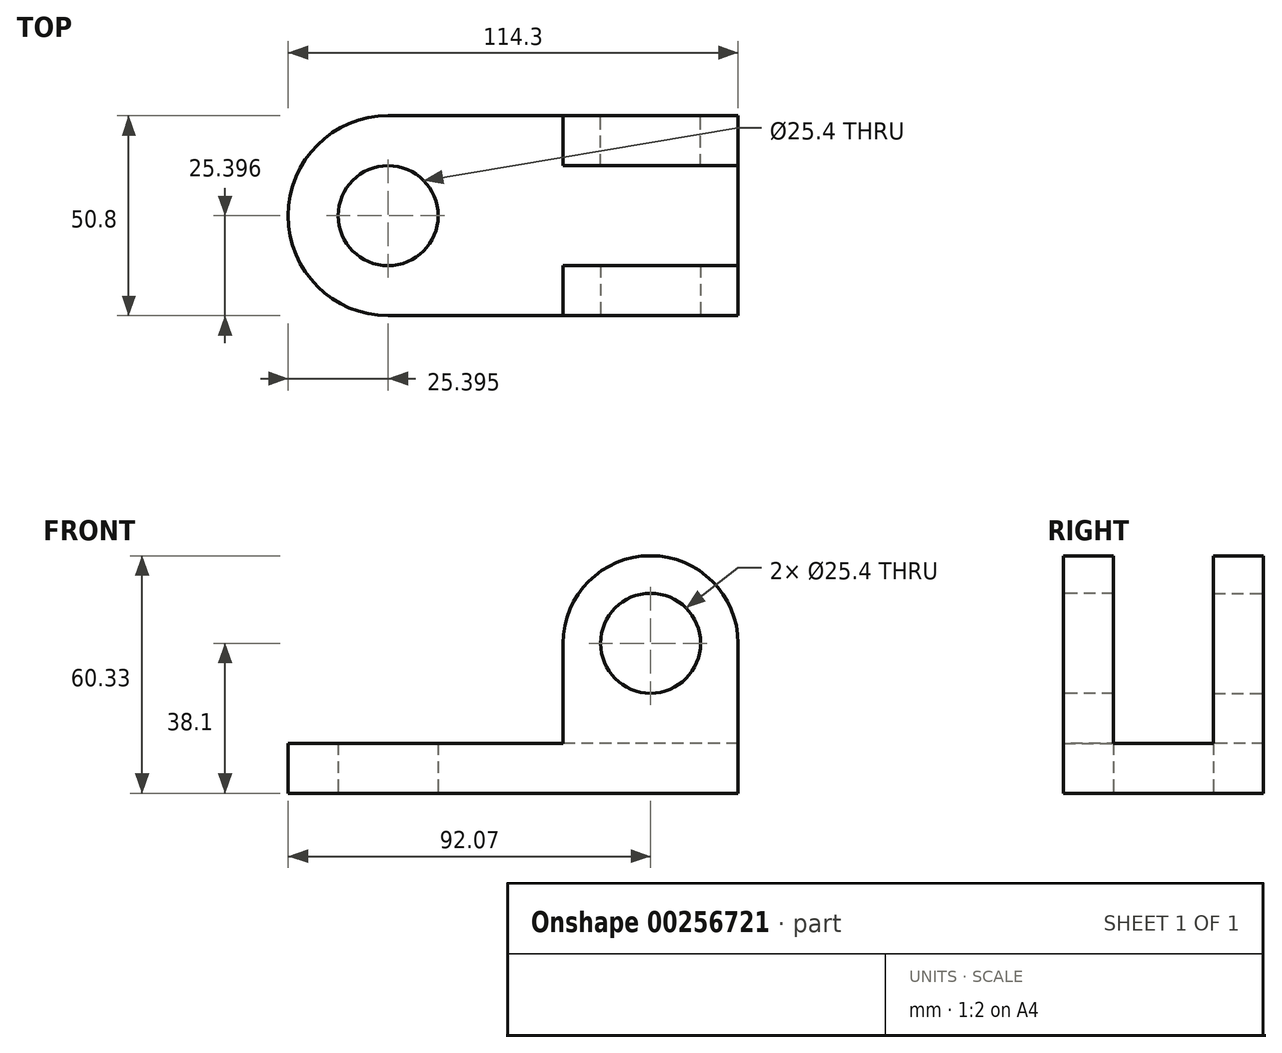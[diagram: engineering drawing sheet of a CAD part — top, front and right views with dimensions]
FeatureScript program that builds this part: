
annotation { "Feature Type Name" : "Feature", "Feature Type Description" : "" }
export const myFeature = defineFeature(function(context is Context, id is Id, definition is map)
    precondition{}
    {
        {
            var Q0;
            Q0=qCreatedBy(makeId("Top.planeOp"),FACE);
            var sketch = newSketch(context, id + "F0", { "sketchPlane" : qUnion([Q0])});
            skLineSegment(sketch, "E0.bottom", {"start": v(50.44, -47.27) * mm, "end": v(-38.46, -47.27) * mm});
            skLineSegment(sketch, "E0.top", {"start": v(50.44, 3.53) * mm, "end": v(-38.46, 3.53) * mm});
            skLineSegment(sketch, "E0.left", {"start": v(50.44, -47.27) * mm, "end": v(50.44, 3.53) * mm});
            skLineSegment(sketch, "E0.right", {"start": v(-38.46, -47.27) * mm, "end": v(-38.46, 3.53) * mm});
            skArc(sketch, "E1", {"start": v(-38.46, 3.53) * mm, "mid": v(-63.86, -21.87) * mm, "end": v(-38.46, -47.27) * mm});
            skCircle(sketch, "E2", {"center": v(-38.46, -21.87) * mm, "radius": 12.7 * mm});
            skSolve(sketch);
        }
        {
            var Q0;
            {var subQ0=sQuery(id+"F0.wireOp",EDGE,"E1");Q0=makeQuery(id+"F0.imprint","IMPRINT",FACE,{"disambiguationData":[TD([[makeQuery(id+"F0.imprint","IMPRINT",EDGE,{"derivedFrom":subQ0}),1.0]])]});}
            extrude(context, id + "F1", {"entities" : qUnion([Q0]), "depth" : 12.7 * mm});
        }
        {
            var Q0;
            {var subQ2=sQuery(id+"F0.wireOp",EDGE,"E0.bottom");Q0=makeQuery(id+"F0.imprint","IMPRINT",FACE,{"disambiguationData":[TD([[makeQuery(id+"F0.imprint","IMPRINT",EDGE,{"derivedFrom":subQ2}),-1.0]])]});}
            extrude(context, id + "F2", {"entities" : qUnion([Q0]), "operationType" : NewBodyOperationType.ADD, "depth" : 12.7 * mm});
        }
        {
            var Q0;
            {var subQ0=sQuery(id+"F0.wireOp",EDGE,"E2");var subQ1=sQuery(id+"F0.wireOp",EDGE,"E0.right");Q0=makeQuery(id+"F2.boolean.opBoolean","MERGE",FACE,{"derivedFrom":[makeQuery(id+"F1.opExtrude","CAP_FACE",FACE,{"disambiguationData":[OSD([subQ1,sQuery(id+"F0.wireOp",EDGE,"E1"),subQ0])],"isStart":false}),makeQuery(id+"F2.opExtrude","CAP_FACE",FACE,{"disambiguationData":[OSD([sQuery(id+"F0.wireOp",EDGE,"E0.bottom"),sQuery(id+"F0.wireOp",EDGE,"E0.top"),sQuery(id+"F0.wireOp",EDGE,"E0.left"),subQ1,subQ0])],"isStart":false})]});}
            var sketch = newSketch(context, id + "F3", { "sketchPlane" : qUnion([Q0])});
            skLineSegment(sketch, "E3", {"start": v(50.44, -21.87) * mm, "end": v(-25.76, -21.87) * mm});
            skLineSegment(sketch, "E4.bottom", {"start": v(50.44, -47.27) * mm, "end": v(5.99, -47.27) * mm});
            skLineSegment(sketch, "E4.top", {"start": v(50.44, -34.57) * mm, "end": v(5.99, -34.57) * mm});
            skLineSegment(sketch, "E4.left", {"start": v(50.44, -47.27) * mm, "end": v(50.44, -34.57) * mm});
            skLineSegment(sketch, "E4.right", {"start": v(5.99, -47.27) * mm, "end": v(5.99, -34.57) * mm});
            skLineSegment(sketch, "E5.MirrorCS", {"start": v(50.44, -9.17) * mm, "end": v(5.99, -9.17) * mm});
            skLineSegment(sketch, "E6.MirrorCS", {"start": v(5.99, 3.53) * mm, "end": v(5.99, -9.17) * mm});
            skLineSegment(sketch, "E7.MirrorCS", {"start": v(50.44, 3.53) * mm, "end": v(5.99, 3.53) * mm});
            skLineSegment(sketch, "E8.MirrorCS", {"start": v(50.44, 3.53) * mm, "end": v(50.44, -9.17) * mm});
            skSolve(sketch);
        }
        {
            var Q0;
            Q0=makeQuery(id+"F3.imprint","IMPRINT",FACE,{"disambiguationData":[TD([[makeQuery(id+"F3.imprint","IMPRINT",EDGE,{"derivedFrom":sQuery(id+"F3.wireOp",EDGE,"E4.bottom")}),-1.0]])]});
            extrude(context, id + "F4", {"entities" : qUnion([Q0]), "operationType" : NewBodyOperationType.ADD, "depth" : 25.4 * mm});
        }
        {
            var Q0;
            Q0=makeQuery(id+"F4.boolean.opBoolean","MERGE",FACE,{"derivedFrom":[makeQuery(id+"F2.opExtrude","SWEPT_FACE",FACE,{"disambiguationData":[OSD([sQuery(id+"F0.wireOp",EDGE,"E0.bottom")])]}),makeQuery(id+"F4.opExtrude","SWEPT_FACE",FACE,{"disambiguationData":[OSD([sQuery(id+"F3.wireOp",EDGE,"E4.bottom")])]})]});
            var sketch = newSketch(context, id + "F5", { "sketchPlane" : qUnion([Q0])});
            skArc(sketch, "E9", {"start": v(50.44, 38.1) * mm, "mid": v(28.21, 60.32) * mm, "end": v(5.99, 38.1) * mm});
            skSolve(sketch);
        }
        {
            var Q0;
            Q0=makeQuery(id+"F5.imprint","IMPRINT",FACE,{"disambiguationData":[TD([[makeQuery(id+"F5.imprint","IMPRINT",EDGE,{"derivedFrom":sQuery(id+"F5.wireOp",EDGE,"E9")}),1.0]])]});
            extrude(context, id + "F6", {"entities" : qUnion([Q0]), "operationType" : NewBodyOperationType.ADD, "oppositeDirection" : true, "depth" : 12.7 * mm});
        }
        {
            var Q0;
            {var subQ0=sQuery(id+"F3.wireOp",EDGE,"E4.bottom");Q0=makeQuery(id+"F6.boolean.opBoolean","MERGE",FACE,{"derivedFrom":[makeQuery(id+"F4.boolean.opBoolean","MERGE",FACE,{"derivedFrom":[makeQuery(id+"F2.opExtrude","SWEPT_FACE",FACE,{"disambiguationData":[OSD([sQuery(id+"F0.wireOp",EDGE,"E0.bottom")])]}),makeQuery(id+"F4.opExtrude","SWEPT_FACE",FACE,{"disambiguationData":[OSD([subQ0])]})]}),makeQuery(id+"F6.opExtrude","CAP_FACE",FACE,{"disambiguationData":[OSD([subQ0,sQuery(id+"F5.wireOp",EDGE,"E9")])],"isStart":true})]});}
            var sketch = newSketch(context, id + "F7", { "sketchPlane" : qUnion([Q0])});
            skCircle(sketch, "E10", {"center": v(28.21, 38.1) * mm, "radius": 12.7 * mm});
            skSolve(sketch);
        }
        {
            var Q0;
            Q0=makeQuery(id+"F7.imprint","IMPRINT",FACE,{"disambiguationData":[TD([[makeQuery(id+"F7.imprint","IMPRINT",EDGE,{"derivedFrom":sQuery(id+"F7.wireOp",EDGE,"E10")}),1.0]])]});
            extrude(context, id + "F8", {"entities" : qUnion([Q0]), "operationType" : NewBodyOperationType.REMOVE, "oppositeDirection" : true, "depth" : 25.4 * mm});
        }
        {
            var Q0;
            Q0=makeQuery(id+"F3.imprint","IMPRINT",FACE,{"disambiguationData":[TD([[makeQuery(id+"F3.imprint","IMPRINT",EDGE,{"derivedFrom":sQuery(id+"F3.wireOp",EDGE,"E5.MirrorCS")}),-1.0]])]});
            extrude(context, id + "F9", {"entities" : qUnion([Q0]), "operationType" : NewBodyOperationType.ADD, "depth" : 25.4 * mm});
        }
        {
            var Q0;
            Q0=makeQuery(id+"F9.boolean.opBoolean","MERGE",FACE,{"derivedFrom":[makeQuery(id+"F2.opExtrude","SWEPT_FACE",FACE,{"disambiguationData":[OSD([sQuery(id+"F0.wireOp",EDGE,"E0.top")])]}),makeQuery(id+"F9.opExtrude","SWEPT_FACE",FACE,{"disambiguationData":[OSD([sQuery(id+"F3.wireOp",EDGE,"E7.MirrorCS")])]})]});
            var sketch = newSketch(context, id + "F10", { "sketchPlane" : qUnion([Q0])});
            skArc(sketch, "E11", {"start": v(-5.99, 38.1) * mm, "mid": v(-28.21, 60.32) * mm, "end": v(-50.44, 38.1) * mm});
            skSolve(sketch);
        }
        {
            var Q0;
            Q0=makeQuery(id+"F10.imprint","IMPRINT",FACE,{"disambiguationData":[TD([[makeQuery(id+"F10.imprint","IMPRINT",EDGE,{"derivedFrom":sQuery(id+"F10.wireOp",EDGE,"E11")}),1.0]])]});
            extrude(context, id + "F11", {"entities" : qUnion([Q0]), "operationType" : NewBodyOperationType.ADD, "oppositeDirection" : true, "depth" : 12.7 * mm});
        }
        {
            var Q0;
            {var subQ0=sQuery(id+"F3.wireOp",EDGE,"E7.MirrorCS");Q0=makeQuery(id+"F11.boolean.opBoolean","MERGE",FACE,{"derivedFrom":[makeQuery(id+"F9.boolean.opBoolean","MERGE",FACE,{"derivedFrom":[makeQuery(id+"F2.opExtrude","SWEPT_FACE",FACE,{"disambiguationData":[OSD([sQuery(id+"F0.wireOp",EDGE,"E0.top")])]}),makeQuery(id+"F9.opExtrude","SWEPT_FACE",FACE,{"disambiguationData":[OSD([subQ0])]})]}),makeQuery(id+"F11.opExtrude","CAP_FACE",FACE,{"disambiguationData":[OSD([subQ0,sQuery(id+"F10.wireOp",EDGE,"E11")])],"isStart":true})]});}
            var sketch = newSketch(context, id + "F12", { "sketchPlane" : qUnion([Q0])});
            skCircle(sketch, "E12", {"center": v(-28.21, 38.1) * mm, "radius": 12.7 * mm});
            skSolve(sketch);
        }
        {
            var Q0;
            Q0=makeQuery(id+"F12.imprint","IMPRINT",FACE,{"disambiguationData":[TD([[makeQuery(id+"F12.imprint","IMPRINT",EDGE,{"derivedFrom":sQuery(id+"F12.wireOp",EDGE,"E12")}),1.0]])]});
            extrude(context, id + "F13", {"entities" : qUnion([Q0]), "operationType" : NewBodyOperationType.REMOVE, "oppositeDirection" : true, "depth" : 25.4 * mm});
        }
    });
